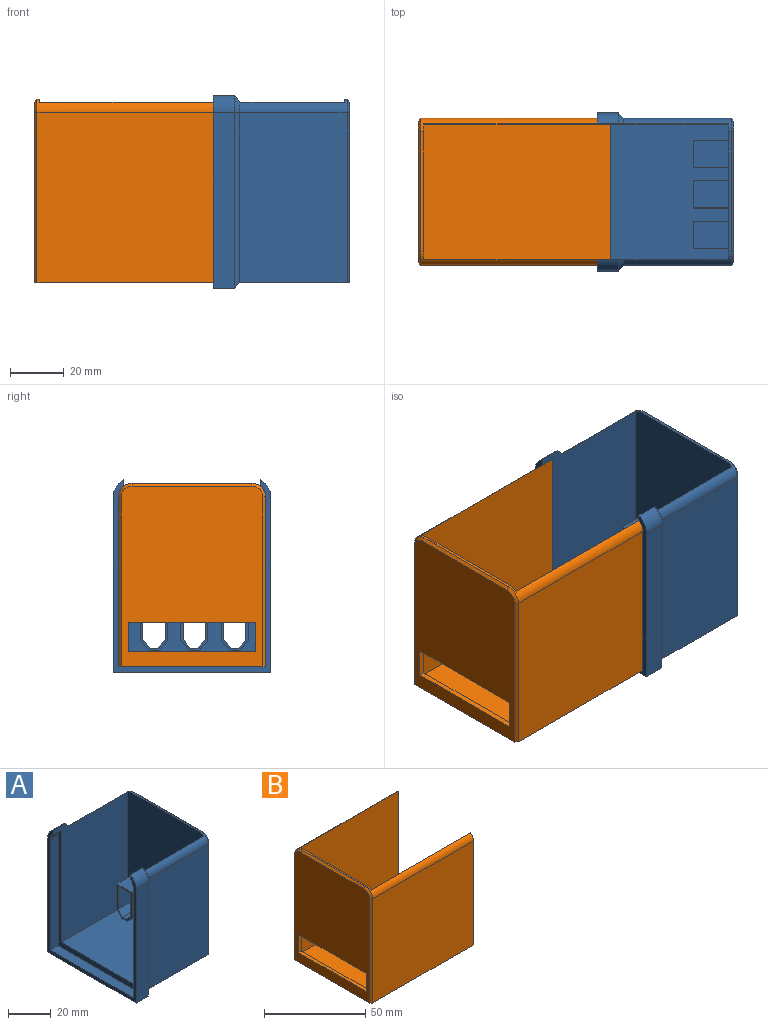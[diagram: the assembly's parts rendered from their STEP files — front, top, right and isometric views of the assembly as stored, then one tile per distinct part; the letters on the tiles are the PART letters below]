
ASSEMBLY  parts=2 mates=1
PART A: 72 faces, bbox 50.9x58.7x71.5 mm
  f0: plane 63x39.71mm, normal (0,1,0), area 2501.7mm2, adj f8,f10,f15,f56
  f1: plane 63x39.71mm, normal (0,-1,0), area 2501.7mm2, adj f8,f9,f11,f54
  f2: plane 66.55x48.93mm, normal (0,-1,0), area 2818.4mm2, adj f3,f7,f10,f41,f44,f50,f52,f57
  f3: plane 65x50.5mm, normal (-1,0,0), area 2771mm2, adj f2,f4,f6,f7,f9,f10,f34,f35
  f4: plane 66.55x48.93mm, normal (0,1,0), area 2818.4mm2, adj f3,f7,f9,f41,f43,f46,f52,f53
  f5: plane 67x52.5mm, normal (1,0,0), area 3133.1mm2, adj f8,f11,f12,f13,f14,f15,f16,f17
  f6: plane 44.5x1mm, normal (0,0,1), area 44.5mm2, adj f3,f9,f10,f13
  f7: plane 50.5x43.71mm, normal (0,0,1), area 2207.3mm2, adj f2,f3,f4,f41
  f8: plane 54.5x40.71mm, normal (0,0,-1), area 2217.7mm2, adj f0,f1,f5,f11,f15,f55
  f9: cylinder r=5mm len=39.71mm, axis (-1,0,0), area 187.3mm2, adj f1,f3,f4,f6,f12,f53
  f10: cylinder r=5mm len=39.71mm, axis (1,0,0), area 187.3mm2, adj f0,f2,f3,f6,f14,f57
  f11: plane 63x1mm, normal (0.71,-0.71,0), area 89.1mm2, adj f1,f5,f8,f12
  f12: cone r=4mm half-angle=45deg, axis (-1,0,0), area 10mm2, adj f5,f9,f11,f13
  f13: plane 44.5x1mm, normal (0.71,0,0.71), area 62.9mm2, adj f5,f6,f12,f14
  f14: cone r=4mm half-angle=45deg, axis (-1,0,0), area 10mm2, adj f5,f10,f13,f15
  f15: plane 63x1mm, normal (0.71,0.71,0), area 89.1mm2, adj f0,f5,f8,f14
  f16: plane 15x13mm, normal (0,-1,0), area 195mm2, adj f5,f17,f21,f71
  f17: plane 15x8.3mm, normal (0,0,-1), area 124.5mm2, adj f5,f16,f18,f71
  f18: plane 15x13mm, normal (0,1,0), area 195mm2, adj f5,f17,f19,f71
  f19: plane 15x3.25mm, normal (0,0.76,0.65), area 64.1mm2, adj f5,f18,f20,f71
  f20: plane 15x2.75mm, normal (0,0,1), area 41.3mm2, adj f5,f19,f21,f71
  f21: plane 15x3.25mm, normal (0,-0.76,0.65), area 64.1mm2, adj f5,f16,f20,f71
  f22: plane 15x13mm, normal (0,-1,0), area 195mm2, adj f5,f23,f27,f64
  f23: plane 15x8.3mm, normal (0,0,-1), area 124.5mm2, adj f5,f22,f24,f64
  f24: plane 15x13mm, normal (0,1,0), area 195mm2, adj f5,f23,f25,f64
  f25: plane 15x3.25mm, normal (0,0.76,0.65), area 64.1mm2, adj f5,f24,f26,f64
  f26: plane 15x2.75mm, normal (0,0,1), area 41.3mm2, adj f5,f25,f27,f64
  f27: plane 15x3.25mm, normal (0,-0.76,0.65), area 64.1mm2, adj f5,f22,f26,f64
  f28: plane 15x3.25mm, normal (0,-0.76,0.65), area 64.1mm2, adj f5,f29,f33,f40
  f29: plane 15x13mm, normal (0,-1,0), area 195mm2, adj f5,f28,f30,f40
  f30: plane 15x8.3mm, normal (0,0,-1), area 124.5mm2, adj f5,f29,f31,f40
  f31: plane 15x13mm, normal (0,1,0), area 195mm2, adj f5,f30,f32,f40
  f32: plane 15x3.25mm, normal (0,0.76,0.65), area 64.1mm2, adj f5,f31,f33,f40
  f33: plane 15x2.75mm, normal (0,0,1), area 41.2mm2, adj f5,f28,f32,f40
  f34: plane 14.23x13mm, normal (0,-1,0), area 185mm2, adj f3,f35,f39,f40
  f35: plane 13x3.82mm, normal (0,-0.76,-0.65), area 65.3mm2, adj f3,f34,f36,f40
  f36: plane 13x3.58mm, normal (0,0,-1), area 46.5mm2, adj f3,f35,f37,f40
  f37: plane 13x3.82mm, normal (0,0.76,-0.65), area 65.3mm2, adj f3,f36,f38,f40
  f38: plane 14.23x13mm, normal (0,1,0), area 185mm2, adj f3,f37,f39,f40
  f39: plane 13x10.1mm, normal (0,0,1), area 131.3mm2, adj f3,f34,f38,f40
  f40: plane 18.05x10.1mm, normal (-1,0,0), area 44mm2, adj f28,f29,f30,f31,f32,f33,f34,f35
  f41: plane 67x54.5mm, normal (-1,0,0), area 414.7mm2, adj f2,f4,f7,f42,f43,f44,f45,f51
  f42: plane 63x5mm, normal (0,-1,0), area 315mm2, adj f41,f44,f51,f52
  f43: cylinder r=5mm len=5mm, axis (1,0,0), area 23.2mm2, adj f4,f41,f45,f52
  f44: cylinder r=5mm len=5mm, axis (1,0,0), area 23.2mm2, adj f2,f41,f42,f52
  f45: plane 63x5mm, normal (0,1,0), area 315mm2, adj f41,f43,f51,f52
  f46: cylinder r=7mm len=8mm, axis (1,0,0), area 63.2mm2, adj f4,f47,f52,f53
  f47: plane 65x8mm, normal (0,-1,0), area 520mm2, adj f46,f48,f52,f54
  f48: plane 58.5x8mm, normal (0,0,-1), area 468mm2, adj f47,f49,f52,f55
  f49: plane 65x8mm, normal (0,1,0), area 520mm2, adj f48,f50,f52,f56
  f50: cylinder r=7mm len=8mm, axis (1,0,0), area 63.2mm2, adj f2,f49,f52,f57
  f51: plane 54.5x5mm, normal (0,0,1), area 272.5mm2, adj f41,f42,f45,f52
  f52: plane 71.32x58.5mm, normal (-1,0,0), area 394.1mm2, adj f2,f4,f42,f43,f44,f45,f46,f47
  f53: cone r=7mm half-angle=45deg, axis (-1,0,0), area 17.5mm2, adj f4,f9,f46,f54
  f54: plane 65x2mm, normal (0.71,-0.71,0), area 181mm2, adj f1,f47,f53,f55
  f55: plane 58.5x2mm, normal (0.71,0,-0.71), area 159.8mm2, adj f8,f48,f54,f56
  f56: plane 65x2mm, normal (0.71,0.71,0), area 181mm2, adj f0,f49,f55,f57
  f57: cone r=7mm half-angle=45deg, axis (-1,0,0), area 17.5mm2, adj f2,f10,f50,f56
  f58: plane 14.23x13mm, normal (0,-1,0), area 185mm2, adj f3,f59,f63,f64
  f59: plane 13x3.82mm, normal (0,-0.76,-0.65), area 65.3mm2, adj f3,f58,f60,f64
  f60: plane 13x3.58mm, normal (0,0,-1), area 46.5mm2, adj f3,f59,f61,f64
  f61: plane 13x3.82mm, normal (0,0.76,-0.65), area 65.3mm2, adj f3,f60,f62,f64
  f62: plane 14.23x13mm, normal (0,1,0), area 185mm2, adj f3,f61,f63,f64
  f63: plane 13x10.1mm, normal (0,0,1), area 131.3mm2, adj f3,f58,f62,f64
  f64: plane 18.05x10.1mm, normal (-1,0,0), area 44mm2, adj f22,f23,f24,f25,f26,f27,f58,f59
  f65: plane 14.23x13mm, normal (0,-1,0), area 185mm2, adj f3,f66,f70,f71
  f66: plane 13x3.82mm, normal (0,-0.76,-0.65), area 65.3mm2, adj f3,f65,f67,f71
  f67: plane 13x3.58mm, normal (0,0,-1), area 46.5mm2, adj f3,f66,f68,f71
  f68: plane 13x3.82mm, normal (0,0.76,-0.65), area 65.3mm2, adj f3,f67,f69,f71
  f69: plane 14.23x13mm, normal (0,1,0), area 185mm2, adj f3,f68,f70,f71
  f70: plane 13x10.1mm, normal (0,0,1), area 131.3mm2, adj f3,f65,f69,f71
  f71: plane 18.05x10.1mm, normal (-1,0,0), area 44mm2, adj f16,f17,f18,f19,f20,f21,f65,f66
PART B: 21 faces, bbox 71.3x54.5x68 mm
  f0: plane 67x54.5mm, normal (1,0,0), area 414.7mm2, adj f13,f14,f15,f16,f17,f18,f19,f20
  f1: plane 47.13x2mm, normal (0,0,-1), area 94.2mm2, adj f2,f4,f7,f10
  f2: plane 10.98x2mm, normal (0,1,0), area 22mm2, adj f1,f3,f7,f10
  f3: plane 47.13x2mm, normal (0,0,1), area 94.2mm2, adj f2,f4,f7,f10
  f4: plane 10.98x2mm, normal (0,-1,0), area 22mm2, adj f1,f3,f7,f10
  f5: plane 44.5x1mm, normal (-0.71,0,0.71), area 62.9mm2, adj f7,f9,f11,f12
  f6: plane 63x1mm, normal (-0.71,0.71,0), area 89.1mm2, adj f7,f12,f13,f20
  f7: plane 67x52.5mm, normal (-1,0,0), area 2993.1mm2, adj f1,f2,f3,f4,f5,f6,f8,f9
  f8: plane 63x1mm, normal (-0.71,-0.71,0), area 89.1mm2, adj f7,f9,f13,f19
  f9: cone r=4mm half-angle=45deg, axis (1,0,0), area 10mm2, adj f5,f7,f8,f15
  f10: plane 65x50.5mm, normal (1,0,0), area 2763.1mm2, adj f1,f2,f3,f4,f11,f14,f15,f16
  f11: plane 44.5x1mm, normal (0,0,1), area 44.5mm2, adj f5,f10,f15,f17
  f12: cone r=4mm half-angle=45deg, axis (1,0,0), area 10mm2, adj f5,f6,f7,f17
  f13: plane 71.29x54.5mm, normal (0,0,-1), area 3884.3mm2, adj f0,f6,f7,f8,f19,f20
  f14: plane 69.29x50.5mm, normal (0,0,1), area 3499.2mm2, adj f0,f10,f16,f18
  f15: cylinder r=5mm len=70.29mm, axis (-1,0,0), area 329.1mm2, adj f0,f9,f10,f11,f16,f19
  f16: plane 69.29x64mm, normal (0,1,0), area 4434.6mm2, adj f0,f10,f14,f15
  f17: cylinder r=5mm len=70.29mm, axis (1,0,0), area 329.1mm2, adj f0,f10,f11,f12,f18,f20
  f18: plane 69.29x64mm, normal (0,-1,0), area 4434.6mm2, adj f0,f10,f14,f17
  f19: plane 70.29x63mm, normal (0,-1,0), area 4428.3mm2, adj f0,f8,f13,f15
  f20: plane 70.29x63mm, normal (0,1,0), area 4428.3mm2, adj f0,f6,f13,f17
PLACE A t=(69.37,51.77,-1.64)mm
PLACE B t=(69.37,51.77,-1.64)mm fixed
MATE slider B.f0 <-> A.f41  axis (1,0,0) through (69.37,62.61,-4.64)mm
